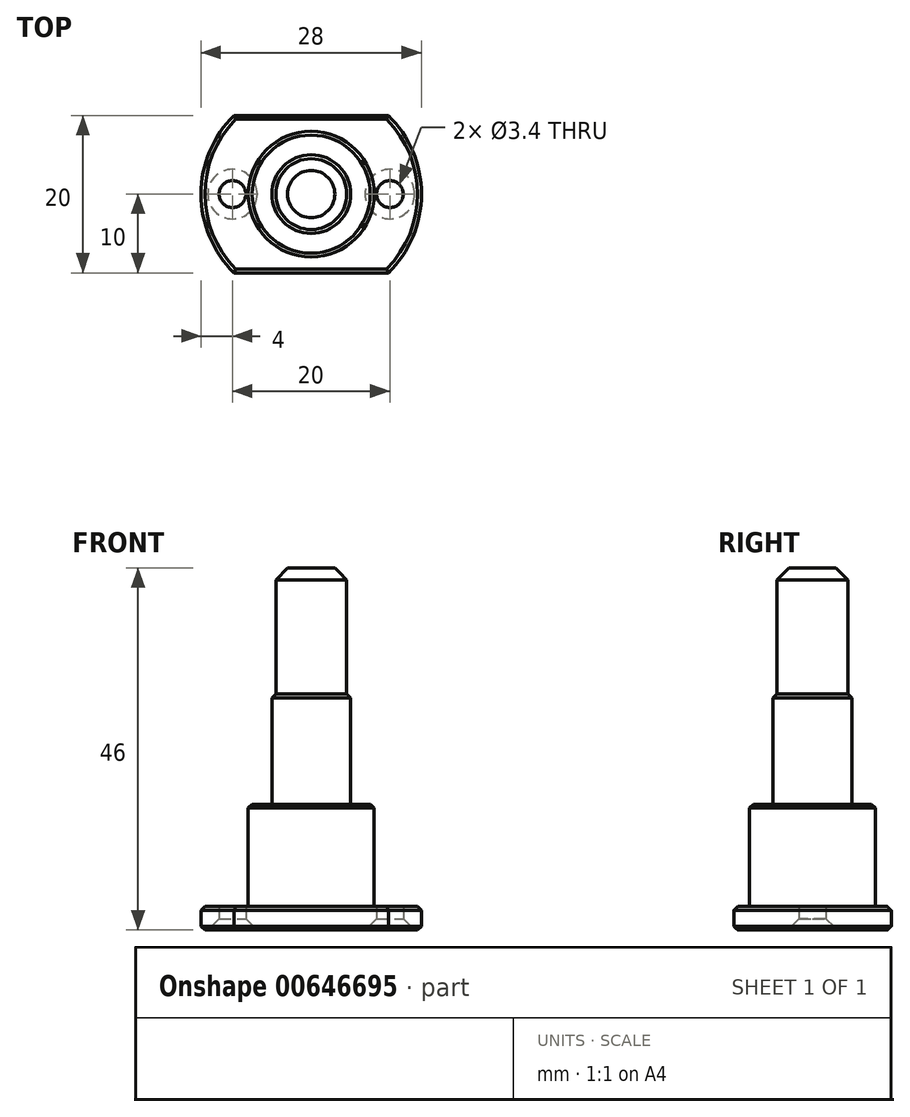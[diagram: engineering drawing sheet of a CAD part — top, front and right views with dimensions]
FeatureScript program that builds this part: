
annotation { "Feature Type Name" : "Feature", "Feature Type Description" : "" }
export const myFeature = defineFeature(function(context is Context, id is Id, definition is map)
    precondition{}
    {
        {
            var Q0;
            Q0=qCreatedBy(makeId("Top.planeOp"),FACE);
            var sketch = newSketch(context, id + "F0", { "sketchPlane" : qUnion([Q0])});
            skArc(sketch, "E0", {"start": v(-9.8, 10) * mm, "mid": v(-14, 0) * mm, "end": v(-9.8, -10) * mm});
            skLineSegment(sketch, "E1", {"start": v(-9.8, 10) * mm, "end": v(9.8, 10) * mm});
            skLineSegment(sketch, "E2.MirrorCS", {"start": v(-9.8, -10) * mm, "end": v(9.8, -10) * mm});
            skArc(sketch, "E3.trimOffspring", {"start": v(9.8, -10) * mm, "mid": v(14, 0) * mm, "end": v(9.8, 10) * mm});
            skPoint(sketch, "E4", {"position": v(-10, 0) * mm});
            skPoint(sketch, "E5.MirrorP", {"position": v(10, 0) * mm});
            skSolve(sketch);
        }
        {
            var Q0;
            Q0=makeQuery(id+"F0.imprint","IMPRINT",FACE,{"disambiguationData":[TD([[makeQuery(id+"F0.imprint","IMPRINT",EDGE,{"derivedFrom":sQuery(id+"F0.wireOp",EDGE,"E0")}),1.0]])]});
            extrude(context, id + "F1", {"entities" : qUnion([Q0]), "depth" : 3 * mm, "offsetDistance" : 25 * mm});
        }
        {
            var Q0;
            Q0=sQuery(id+"F0.wireOp",VERTEX,"E4");
            var Q1;
            Q1=sQuery(id+"F0.wireOp",VERTEX,"E5.MirrorP");
            var Q2;
            Q2=makeQuery(id+"F1.opExtrude","SWEPT_BODY",BODY,{"disambiguationData":[OSD([sQuery(id+"F0.wireOp",EDGE,"E0"),sQuery(id+"F0.wireOp",EDGE,"E1"),sQuery(id+"F0.wireOp",EDGE,"E2.MirrorCS"),sQuery(id+"F0.wireOp",EDGE,"E3.trimOffspring")])]});
            hole(context, id + "F2", {"style" : HoleStyle.C_SINK, "endStyle" : HoleEndStyle.THROUGH, "oppositeDirection" : true, "holeDiameter" : 3.4 * mm, "cSinkDiameter" : 6.3 * mm, "cSinkAngle" : 90 * degree, "majorDiameter" : 5 * mm, "isTappedThrough" : true, "tappedDepth" : 12 * mm, "tapClearance" : 3, "locations" : qUnion([Q0, Q1]), "scope" : qUnion([Q2])});
        }
        {
            var Q0;
            Q0=makeQuery(id+"F1.opExtrude","CAP_FACE",FACE,{"disambiguationData":[OSD([sQuery(id+"F0.wireOp",EDGE,"E0"),sQuery(id+"F0.wireOp",EDGE,"E1"),sQuery(id+"F0.wireOp",EDGE,"E2.MirrorCS"),sQuery(id+"F0.wireOp",EDGE,"E3.trimOffspring")])],"isStart":false});
            var sketch = newSketch(context, id + "F3", { "sketchPlane" : qUnion([Q0])});
            skCircle(sketch, "E6", {"center": v(0, 0) * mm, "radius": 8 * mm});
            skSolve(sketch);
        }
        {
            var Q0;
            Q0=makeQuery(id+"F3.imprint","IMPRINT",FACE,{"disambiguationData":[TD([[makeQuery(id+"F3.imprint","IMPRINT",EDGE,{"derivedFrom":sQuery(id+"F3.wireOp",EDGE,"E6")}),1.0]])]});
            extrude(context, id + "F4", {"entities" : qUnion([Q0]), "operationType" : NewBodyOperationType.ADD, "depth" : 13 * mm, "offsetDistance" : 25 * mm});
        }
        {
            var Q0;
            Q0=makeQuery(id+"F4.opExtrude","CAP_FACE",FACE,{"disambiguationData":[OSD([sQuery(id+"F3.wireOp",EDGE,"E6")])],"isStart":false});
            var sketch = newSketch(context, id + "F5", { "sketchPlane" : qUnion([Q0])});
            skCircle(sketch, "E7", {"center": v(0, 0) * mm, "radius": 5 * mm});
            skSolve(sketch);
        }
        {
            var Q0;
            Q0=makeQuery(id+"F5.imprint","IMPRINT",FACE,{"disambiguationData":[TD([[makeQuery(id+"F5.imprint","IMPRINT",EDGE,{"derivedFrom":sQuery(id+"F5.wireOp",EDGE,"E7")}),1.0]])]});
            extrude(context, id + "F6", {"entities" : qUnion([Q0]), "operationType" : NewBodyOperationType.ADD, "depth" : (30 - 16) * mm, "offsetDistance" : 25 * mm});
        }
        {
            var Q0;
            Q0=makeQuery(id+"F6.opExtrude","CAP_FACE",FACE,{"disambiguationData":[OSD([sQuery(id+"F5.wireOp",EDGE,"E7")])],"isStart":false});
            var sketch = newSketch(context, id + "F7", { "sketchPlane" : qUnion([Q0])});
            skCircle(sketch, "E8", {"center": v(0, 0) * mm, "radius": 4.5 * mm});
            skSolve(sketch);
        }
        {
            var Q0;
            Q0=makeQuery(id+"F7.imprint","IMPRINT",FACE,{"disambiguationData":[TD([[makeQuery(id+"F7.imprint","IMPRINT",EDGE,{"derivedFrom":sQuery(id+"F7.wireOp",EDGE,"E8")}),1.0]])]});
            extrude(context, id + "F8", {"entities" : qUnion([Q0]), "operationType" : NewBodyOperationType.ADD, "depth" : 16 * mm, "offsetDistance" : 25 * mm});
        }
        {
            var Q0;
            Q0=makeQuery(id+"F8.opExtrude","CAP_EDGE",EDGE,{"disambiguationData":[OSD([sQuery(id+"F7.wireOp",EDGE,"E8")])],"isStart":false});
            chamfer(context, id + "F9", {"entities" : qUnion([Q0]), "width" : 1.5 * mm, "tangentPropagation" : true});
        }
        {
            var Q0;
            Q0=makeQuery(id+"F6.opExtrude","CAP_EDGE",EDGE,{"disambiguationData":[OSD([sQuery(id+"F5.wireOp",EDGE,"E7")])],"isStart":false});
            var Q1;
            Q1=makeQuery(id+"F1.opExtrude","CAP_EDGE",EDGE,{"disambiguationData":[OSD([sQuery(id+"F0.wireOp",EDGE,"E2.MirrorCS")])],"isStart":false});
            var Q2;
            Q2=makeQuery(id+"F1.opExtrude","CAP_EDGE",EDGE,{"disambiguationData":[OSD([sQuery(id+"F0.wireOp",EDGE,"E3.trimOffspring")])],"isStart":false});
            var Q3;
            Q3=makeQuery(id+"F1.opExtrude","CAP_EDGE",EDGE,{"disambiguationData":[OSD([sQuery(id+"F0.wireOp",EDGE,"E1")])],"isStart":false});
            var Q4;
            Q4=makeQuery(id+"F1.opExtrude","CAP_EDGE",EDGE,{"disambiguationData":[OSD([sQuery(id+"F0.wireOp",EDGE,"E0")])],"isStart":false});
            var Q5;
            Q5=makeQuery(id+"F1.opExtrude","CAP_EDGE",EDGE,{"disambiguationData":[OSD([sQuery(id+"F0.wireOp",EDGE,"E0")])],"isStart":true});
            var Q6;
            Q6=makeQuery(id+"F1.opExtrude","CAP_EDGE",EDGE,{"disambiguationData":[OSD([sQuery(id+"F0.wireOp",EDGE,"E2.MirrorCS")])],"isStart":true});
            var Q7;
            Q7=makeQuery(id+"F1.opExtrude","CAP_EDGE",EDGE,{"disambiguationData":[OSD([sQuery(id+"F0.wireOp",EDGE,"E3.trimOffspring")])],"isStart":true});
            var Q8;
            Q8=makeQuery(id+"F1.opExtrude","CAP_EDGE",EDGE,{"disambiguationData":[OSD([sQuery(id+"F0.wireOp",EDGE,"E1")])],"isStart":true});
            var Q9;
            Q9=makeQuery(id+"F4.opExtrude","CAP_EDGE",EDGE,{"disambiguationData":[OSD([sQuery(id+"F3.wireOp",EDGE,"E6")])],"isStart":false});
            chamfer(context, id + "F10", {"entities" : qUnion([Q0, Q1, Q2, Q3, Q4, Q5, Q6, Q7, Q8, Q9]), "width" : 0.5 * mm, "tangentPropagation" : true});
        }
    });
